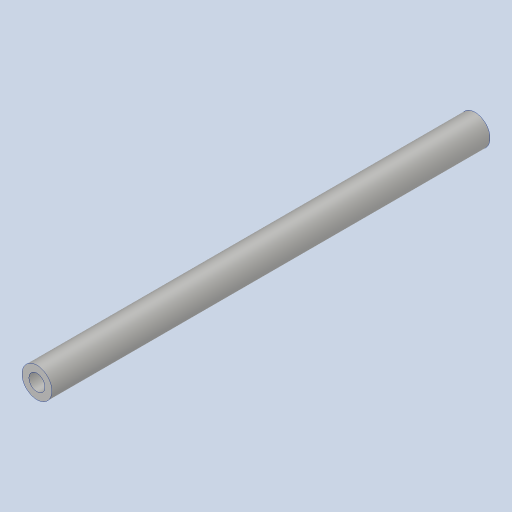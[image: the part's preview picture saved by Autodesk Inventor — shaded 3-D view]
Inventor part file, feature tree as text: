
AUTODESK INVENTOR PART (.ipt)
format: ipt  version: 2023.4 (Build 274418000, 418)  size: 96,768 bytes
history: native  units: in
note: dims shown in document units (in); Inventor stores cm internally (conversion verified against a paired STEP export)
features: extrude x1, hole x1
ambient origin geometry x8: Origin, YZ Plane, XZ Plane, XY Plane, X Axis, Y Axis, Z Axis, Center Point
bodies: Solid1 (feature_tree)
feature tree (2):
  extrude  "Extrusion1"  Depth=5.5in
  hole  "Hole1"  [1 undecoded]
note: 1 required parameter value undecoded (feature->parameter linkage not recoverable at this tier; creation-order binding heuristic only, values carry confidence <= 0.55)
